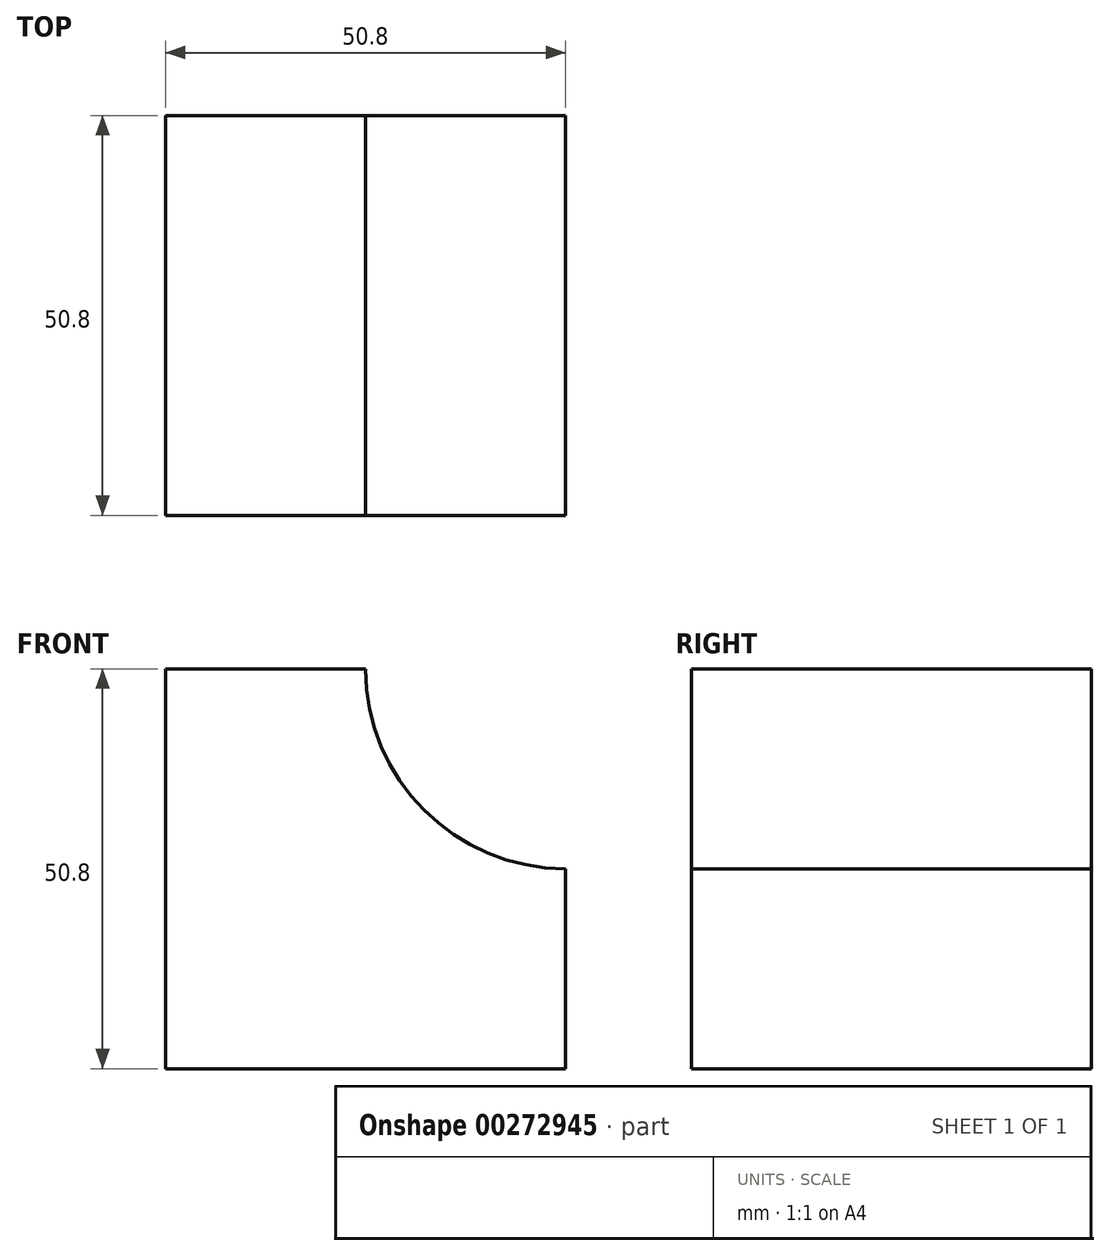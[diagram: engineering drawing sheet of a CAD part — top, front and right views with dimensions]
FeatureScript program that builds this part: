
annotation { "Feature Type Name" : "Feature", "Feature Type Description" : "" }
export const myFeature = defineFeature(function(context is Context, id is Id, definition is map)
    precondition{}
    {
        {
            var Q0;
            Q0=qCreatedBy(makeId("Front.planeOp"),FACE);
            var sketch = newSketch(context, id + "F0", { "sketchPlane" : qUnion([Q0])});
            skLineSegment(sketch, "E0", {"start": v(0, 0) * mm, "end": v(-50.8, 0) * mm});
            skLineSegment(sketch, "E1", {"start": v(-50.8, 0) * mm, "end": v(-50.8, 50.8) * mm});
            skLineSegment(sketch, "E2", {"start": v(-50.8, 50.8) * mm, "end": v(-25.4, 50.8) * mm});
            skLineSegment(sketch, "E3", {"start": v(-25.4, 50.8) * mm, "end": v(-25.4, 25.4) * mm});
            skLineSegment(sketch, "E4", {"start": v(-25.4, 25.4) * mm, "end": v(0, 25.4) * mm});
            skLineSegment(sketch, "E5", {"start": v(0, 25.4) * mm, "end": v(0, 0) * mm});
            skArc(sketch, "E6", {"start": v(-25.4, 50.8) * mm, "mid": v(-17.96, 32.84) * mm, "end": v(0, 25.4) * mm});
            skSolve(sketch);
        }
        {
            var Q0;
            Q0=makeQuery(id+"F0.imprint","IMPRINT",FACE,{"disambiguationData":[TD([[makeQuery(id+"F0.imprint","IMPRINT",EDGE,{"derivedFrom":sQuery(id+"F0.wireOp",EDGE,"E0")}),-1.0]])]});
            extrude(context, id + "F1", {"entities" : qUnion([Q0]), "depth" : 50.8 * mm});
        }
        {
            var Q0;
            Q0=makeQuery(id+"F0.imprint","IMPRINT",FACE,{"disambiguationData":[TD([[makeQuery(id+"F0.imprint","IMPRINT",EDGE,{"derivedFrom":sQuery(id+"F0.wireOp",EDGE,"E0")}),-1.0]])]});
            var Q1;
            Q1=makeQuery(id+"F0.imprint","IMPRINT",FACE,{"disambiguationData":[TD([[makeQuery(id+"F0.imprint","IMPRINT",EDGE,{"derivedFrom":sQuery(id+"F0.wireOp",EDGE,"E3")}),1.0]])]});
            extrude(context, id + "F2", {"entities" : qUnion([Q0, Q1]), "operationType" : NewBodyOperationType.ADD, "depth" : 50.8 * mm});
        }
    });
